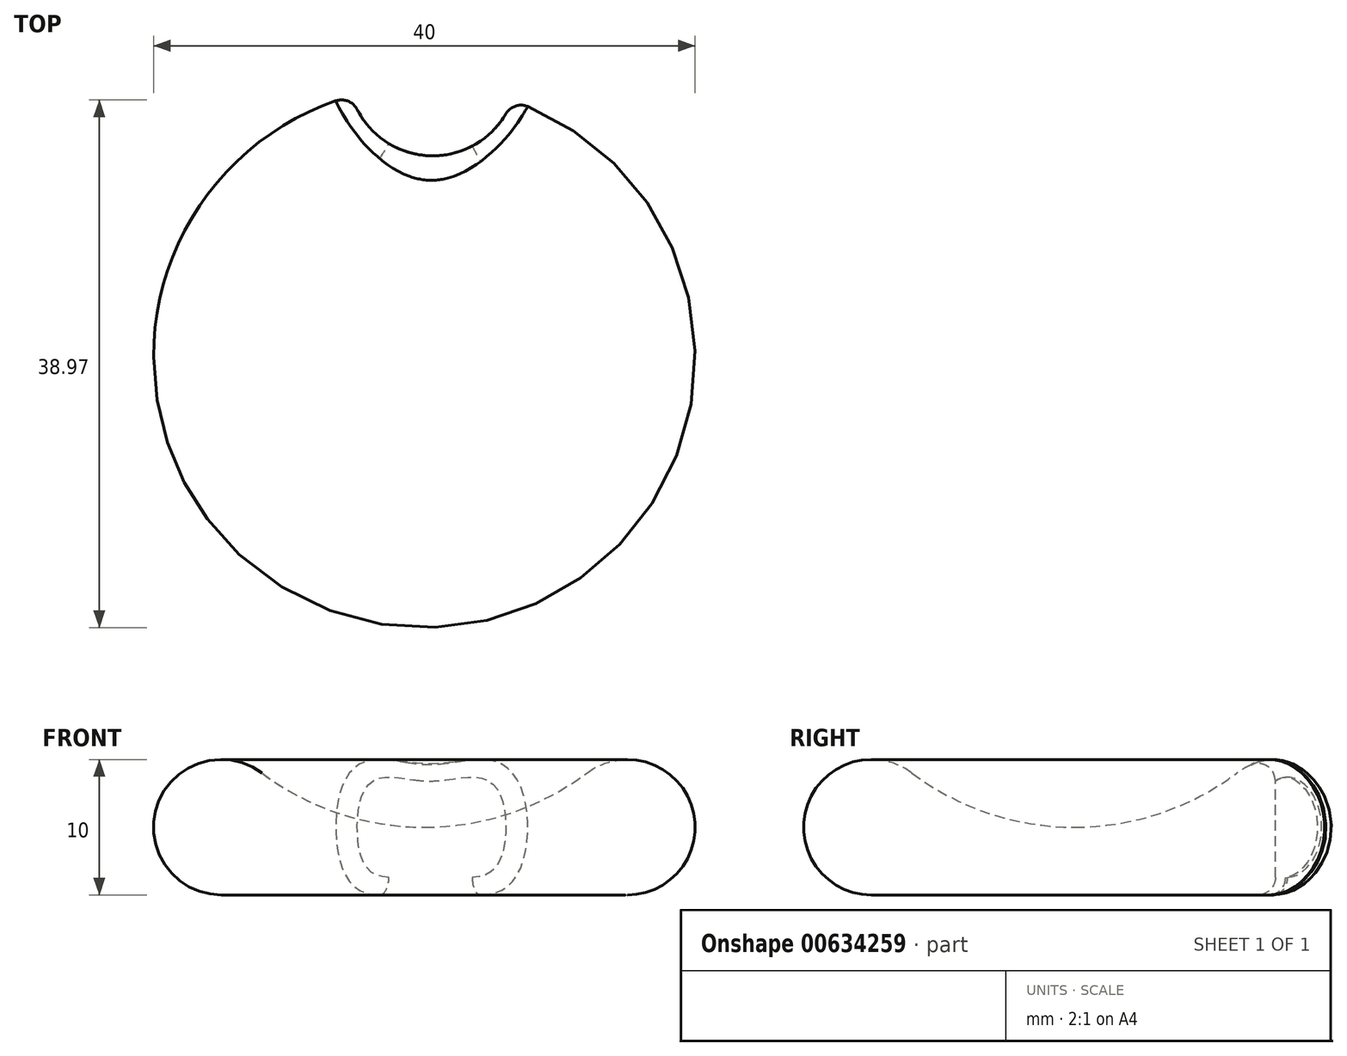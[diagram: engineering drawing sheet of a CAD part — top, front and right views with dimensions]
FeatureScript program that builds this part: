
annotation { "Feature Type Name" : "Feature", "Feature Type Description" : "" }
export const myFeature = defineFeature(function(context is Context, id is Id, definition is map)
    precondition{}
    {
        {
            var Q0;
            Q0=qCreatedBy(makeId("Front.planeOp"),FACE);
            var sketch = newSketch(context, id + "F0", { "sketchPlane" : qUnion([Q0])});
            skArc(sketch, "E0", {"start": v(-12, 9) * mm, "mid": v(-19.74, 6.58) * mm, "end": v(-15, 0) * mm});
            skArc(sketch, "E1", {"start": v(-12, 9) * mm, "mid": v(-6.32, 6.03) * mm, "end": v(0, 5) * mm});
            skLineSegment(sketch, "E2", {"start": v(-15, 0) * mm, "end": v(0, 0) * mm});
            skLineSegment(sketch, "E3", {"start": v(0, 0) * mm, "end": v(0, 5) * mm});
            skSolve(sketch);
        }
        {
            var Q0;
            Q0 = qSketchRegion(id + "F0", true);
            var Q1;
            Q1=sQuery(id+"F0.wireOp",EDGE,"E3");
            revolve(context, id + "F1", {"entities" : qUnion([Q0]), "axis" : qUnion([Q1]), "revolveType" : RevolveType.FULL});
        }
        {
            var Q0;
            Q0=qCreatedBy(makeId("Top.planeOp"),FACE);
            cPlane(context, id + "F2", {"entities" : qUnion([Q0]), "cplaneType" : CPlaneType.OFFSET, "offset" : 10 * mm, "width" : 152.4 * mm, "height" : 152.4 * mm});
        }
        {
            var Q0;
            Q0=qCreatedBy(id+"F2.planeOp",FACE);
            var sketch = newSketch(context, id + "F3", { "sketchPlane" : qUnion([Q0])});
            skCircle(sketch, "E4", {"center": v(0.62, 21.1) * mm, "radius": 6.26 * mm});
            skSolve(sketch);
        }
        {
            var Q0;
            Q0=makeQuery(id+"F3.imprint","IMPRINT",FACE,{"disambiguationData":[TD([[makeQuery(id+"F3.imprint","IMPRINT",EDGE,{"derivedFrom":sQuery(id+"F3.wireOp",EDGE,"E4")}),1.0]])]});
            var Q1;
            Q1=sQuery(id+"F3.wireOp",EDGE,"E4");
            extrude(context, id + "F4", {"entities" : qUnion([Q0]), "operationType" : NewBodyOperationType.REMOVE, "surfaceEntities" : qUnion([Q1]), "oppositeDirection" : true, "depth" : 25.4 * mm, "offsetDistance" : 25.4 * mm});
        }
        {
            var Q0;
            Q0=makeQuery(id+"F4.boolean.opBoolean","COPY",FACE,{"derivedFrom":makeQuery(id+"F4.opExtrude","SWEPT_FACE",FACE,{"disambiguationData":[OSD([sQuery(id+"F3.wireOp",EDGE,"E4")])]})});
            fillet(context, id + "F5", {"entities" : qUnion([Q0]), "radius" : 1.3 * mm, "tangentPropagation" : true, "allowEdgeOverflow" : false});
        }
    });
